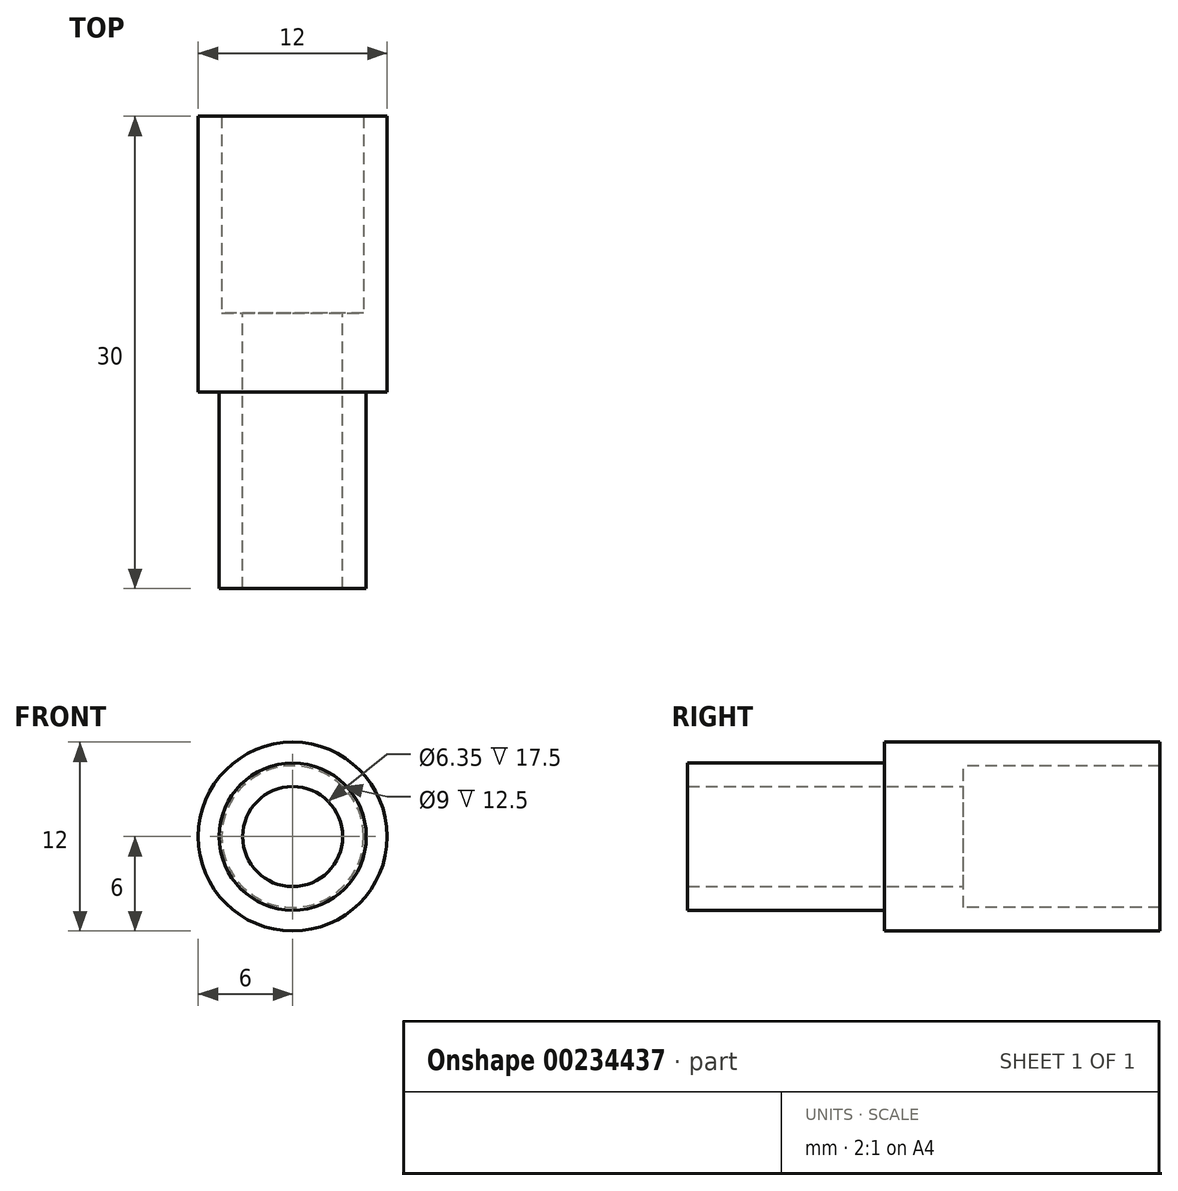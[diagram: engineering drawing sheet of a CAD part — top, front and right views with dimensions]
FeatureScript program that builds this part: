
annotation { "Feature Type Name" : "Feature", "Feature Type Description" : "" }
export const myFeature = defineFeature(function(context is Context, id is Id, definition is map)
    precondition{}
    {
        {
            var Q0;
            Q0=qCreatedBy(makeId("Front.planeOp"),FACE);
            var sketch = newSketch(context, id + "F0", { "sketchPlane" : qUnion([Q0])});
            skCircle(sketch, "E0", {"center": v(0, 0) * mm, "radius": 3.17 * mm});
            skCircle(sketch, "E1", {"center": v(0, 0) * mm, "radius": 4.68 * mm});
            skSolve(sketch);
        }
        {
            var Q0;
            Q0 = qSketchRegion(id + "F0", true);
            extrude(context, id + "F1", {"entities" : qUnion([Q0]), "depth" : 15 * mm, "offsetDistance" : 25 * mm, "hasSecondDirection" : true, "secondDirectionOppositeDirection" : true, "secondDirectionDepth" : 2.5 * mm});
        }
        {
            var Q0;
            Q0=qCreatedBy(makeId("Front.planeOp"),FACE);
            var sketch = newSketch(context, id + "F2", { "sketchPlane" : qUnion([Q0])});
            skCircle(sketch, "E2", {"center": v(0, 0) * mm, "radius": 4.5 * mm});
            skCircle(sketch, "E3", {"center": v(0, 0) * mm, "radius": 6 * mm});
            skSolve(sketch);
        }
        {
            var Q0;
            Q0 = qSketchRegion(id + "F2", true);
            extrude(context, id + "F3", {"entities" : qUnion([Q0]), "operationType" : NewBodyOperationType.ADD, "oppositeDirection" : true, "depth" : 15 * mm, "offsetDistance" : 25 * mm, "hasSecondDirection" : true, "secondDirectionOppositeDirection" : false, "secondDirectionDepth" : 2.5 * mm});
        }
    });
